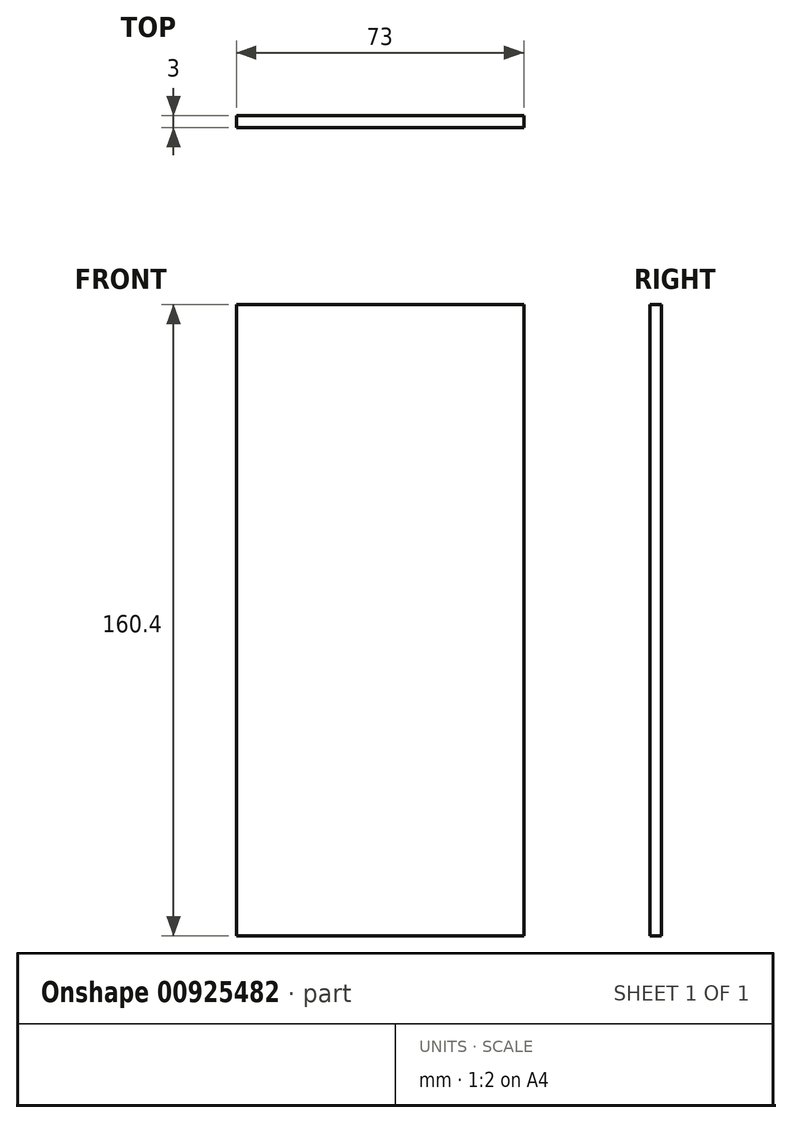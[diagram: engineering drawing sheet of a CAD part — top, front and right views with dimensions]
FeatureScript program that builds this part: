
annotation { "Feature Type Name" : "Feature", "Feature Type Description" : "" }
export const myFeature = defineFeature(function(context is Context, id is Id, definition is map)
    precondition{}
    {
        {
            var Q0;
            Q0=qCreatedBy(makeId("Front.planeOp"),FACE);
            var sketch = newSketch(context, id + "F0", { "sketchPlane" : qUnion([Q0])});
            skLineSegment(sketch, "E0.bottom", {"start": v(0, 0) * mm, "end": v(73, 0) * mm});
            skLineSegment(sketch, "E0.top", {"start": v(0, 160.4) * mm, "end": v(73, 160.4) * mm});
            skLineSegment(sketch, "E0.left", {"start": v(0, 0) * mm, "end": v(0, 160.4) * mm});
            skLineSegment(sketch, "E0.right", {"start": v(73, 0) * mm, "end": v(73, 160.4) * mm});
            skSolve(sketch);
        }
        {
            var Q0;
            Q0 = qSketchRegion(id + "F0", true);
            extrude(context, id + "F1", {"entities" : qUnion([Q0]), "depth" : 3 * mm, "offsetDistance" : 25 * mm});
        }
    });
